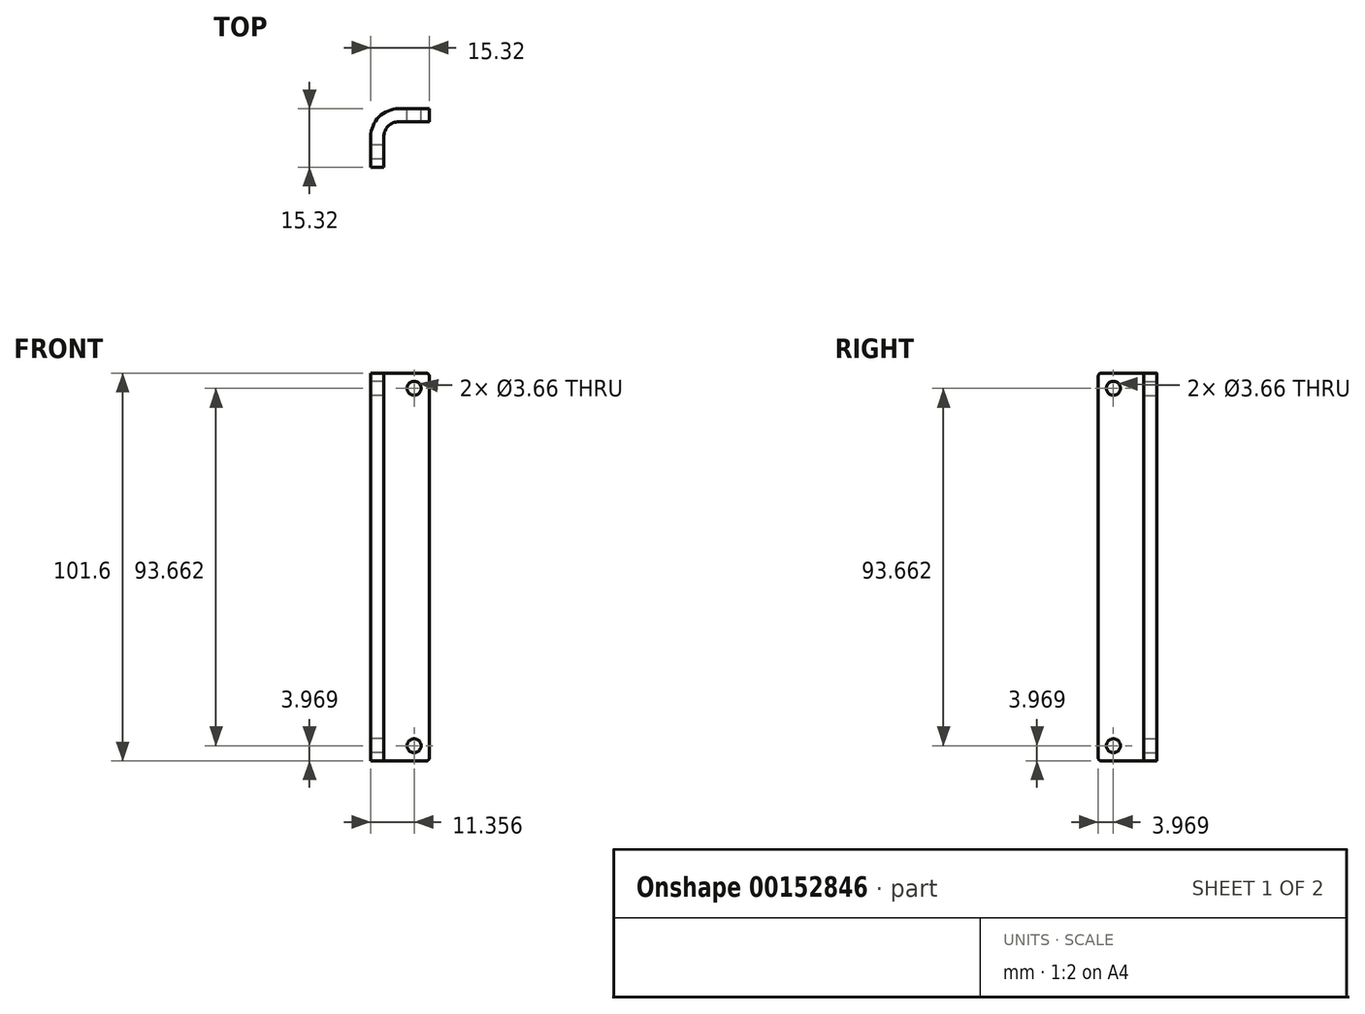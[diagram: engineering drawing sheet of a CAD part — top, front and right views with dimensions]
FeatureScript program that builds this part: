
annotation { "Feature Type Name" : "Feature", "Feature Type Description" : "" }
export const myFeature = defineFeature(function(context is Context, id is Id, definition is map)
    precondition{}
    {
        {
            var Q0;
            Q0=qCreatedBy(makeId("Top.planeOp"),FACE);
            var sketch = newSketch(context, id + "F0", { "sketchPlane" : qUnion([Q0])});
            skLineSegment(sketch, "E0.bottom", {"start": v(0, 0) * mm, "end": v(-3.42, 0) * mm});
            skLineSegment(sketch, "E1.left", {"start": v(0, 0) * mm, "end": v(0, 11.9) * mm});
            skLineSegment(sketch, "E1.right", {"start": v(-3.42, 0) * mm, "end": v(-3.42, 15.32) * mm});
            skLineSegment(sketch, "E2.bottom", {"start": v(0, 11.9) * mm, "end": v(11.9, 11.9) * mm});
            skLineSegment(sketch, "E2.top", {"start": v(-3.42, 15.32) * mm, "end": v(11.9, 15.32) * mm});
            skLineSegment(sketch, "E3", {"start": v(0, 11.9) * mm, "end": v(-3.42, 11.9) * mm, "construction": true});
            skLineSegment(sketch, "E4", {"start": v(0, 11.9) * mm, "end": v(0, 15.32) * mm, "construction": true});
            skLineSegment(sketch, "E5", {"start": v(11.9, 11.9) * mm, "end": v(11.9, 15.32) * mm});
            skSolve(sketch);
        }
        {
            var Q0;
            Q0=qSketchRegion(id+"F0",true);
            extrude(context, id + "F1", {"entities" : qUnion([Q0]), "depth" : 101.6 * mm});
        }
        {
            var Q0;
            Q0=makeQuery(id+"F1.opExtrude","SWEPT_EDGE",EDGE,{"disambiguationData":[OSD([sQuery(id+"F0.wireOp",EDGE,"E1.left"),sQuery(id+"F0.wireOp",EDGE,"E2.bottom")])]});
            fillet(context, id + "F2", {"entities" : qUnion([Q0]), "radius" : 3.97 * mm, "tangentPropagation" : true, "allowEdgeOverflow" : false});
        }
        {
            var Q0;
            Q0=makeQuery(id+"F1.opExtrude","SWEPT_EDGE",EDGE,{"disambiguationData":[OSD([sQuery(id+"F0.wireOp",EDGE,"E1.right"),sQuery(id+"F0.wireOp",EDGE,"E2.top")])]});
            fillet(context, id + "F3", {"entities" : qUnion([Q0]), "radius" : 7.39 * mm, "tangentPropagation" : true, "allowEdgeOverflow" : false});
        }
        {
            var Q0;
            Q0=makeQuery(id+"F1.opExtrude","SWEPT_FACE",FACE,{"disambiguationData":[OSD([sQuery(id+"F0.wireOp",EDGE,"E2.top")])]});
            var sketch = newSketch(context, id + "F4", { "sketchPlane" : qUnion([Q0])});
            skLineSegment(sketch, "E6", {"start": v(-7.94, 101.6) * mm, "end": v(-7.94, 97.63) * mm, "construction": true});
            skLineSegment(sketch, "E7", {"start": v(-7.94, 97.63) * mm, "end": v(-11.9, 97.63) * mm, "construction": true});
            skLineSegment(sketch, "E8", {"start": v(-7.94, 0) * mm, "end": v(-7.94, 3.97) * mm, "construction": true});
            skCircle(sketch, "E9", {"center": v(-7.94, 97.63) * mm, "radius": 1.83 * mm});
            skCircle(sketch, "E10", {"center": v(-7.94, 3.97) * mm, "radius": 1.83 * mm});
            skSolve(sketch);
        }
        {
            var Q0;
            Q0 = qSketchRegion(id + "F4", true);
            var Q1;
            Q1=makeQuery(id+"F1.opExtrude","SWEPT_FACE",FACE,{"disambiguationData":[OSD([sQuery(id+"F0.wireOp",EDGE,"E2.bottom")])]});
            extrude(context, id + "F5", {"entities" : qUnion([Q0]), "operationType" : NewBodyOperationType.REMOVE, "endBound" : BoundingType.UP_TO_SURFACE, "oppositeDirection" : true, "endBoundEntityFace" : qUnion([Q1]), "depth" : 25.4 * mm});
        }
        {
            var Q0;
            Q0=makeQuery(id+"F1.opExtrude","SWEPT_FACE",FACE,{"disambiguationData":[OSD([sQuery(id+"F0.wireOp",EDGE,"E1.right")])]});
            var sketch = newSketch(context, id + "F6", { "sketchPlane" : qUnion([Q0])});
            skLineSegment(sketch, "E11", {"start": v(-3.97, 101.6) * mm, "end": v(-3.97, 97.63) * mm, "construction": true});
            skLineSegment(sketch, "E12", {"start": v(-3.97, 97.63) * mm, "end": v(0, 97.63) * mm, "construction": true});
            skLineSegment(sketch, "E13", {"start": v(-3.97, 0) * mm, "end": v(-3.97, 3.97) * mm, "construction": true});
            skCircle(sketch, "E14", {"center": v(-3.97, 97.63) * mm, "radius": 1.83 * mm});
            skCircle(sketch, "E15", {"center": v(-3.97, 3.97) * mm, "radius": 1.83 * mm});
            skSolve(sketch);
        }
        {
            var Q0;
            Q0 = qSketchRegion(id + "F6", true);
            var Q1;
            Q1=makeQuery(id+"F1.opExtrude","SWEPT_FACE",FACE,{"disambiguationData":[OSD([sQuery(id+"F0.wireOp",EDGE,"E1.left")])]});
            extrude(context, id + "F7", {"entities" : qUnion([Q0]), "operationType" : NewBodyOperationType.REMOVE, "endBound" : BoundingType.UP_TO_SURFACE, "oppositeDirection" : true, "endBoundEntityFace" : qUnion([Q1]), "depth" : 25.4 * mm});
        }
        {
            var Q0;
            Q0=makeQuery(id+"F1.opExtrude","CAP_EDGE",EDGE,{"disambiguationData":[OSD([sQuery(id+"F0.wireOp",EDGE,"E0.bottom")])],"isStart":false});
            var Q1;
            Q1=makeQuery(id+"F1.opExtrude","CAP_EDGE",EDGE,{"disambiguationData":[OSD([sQuery(id+"F0.wireOp",EDGE,"E5")])],"isStart":false});
            var Q2;
            Q2=makeQuery(id+"F1.opExtrude","CAP_EDGE",EDGE,{"disambiguationData":[OSD([sQuery(id+"F0.wireOp",EDGE,"E5")])],"isStart":true});
            var Q3;
            Q3=makeQuery(id+"F1.opExtrude","CAP_EDGE",EDGE,{"disambiguationData":[OSD([sQuery(id+"F0.wireOp",EDGE,"E0.bottom")])],"isStart":true});
            fillet(context, id + "F8", {"entities" : qUnion([Q0, Q1, Q2, Q3]), "radius" : 0.76 * mm, "tangentPropagation" : true, "allowEdgeOverflow" : false});
        }
    });
